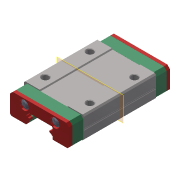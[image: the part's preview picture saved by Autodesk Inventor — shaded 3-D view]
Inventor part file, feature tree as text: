
AUTODESK INVENTOR PART (.ipt)
format: ipt  version: 2019.4 (Build 234330000, 330)  size: 473,600 bytes
history: imported  units: mm
features: other x9, plane x1, imported_body x1
ambient origin geometry x8: Origin, YZ Plane, XZ Plane, XY Plane, X Axis, Y Axis, Z Axis, Center Point
bodies: Solid1 (imported_parasolid), Solid2 (imported_parasolid), Solid3 (imported_parasolid), Solid4 (imported_parasolid), Solid5 (imported_parasolid), Solid6 (imported_parasolid), Solid7 (imported_parasolid), Solid8 (imported_parasolid), Solid9 (imported_parasolid)
feature tree (11):
  plane  "Work Plane1"
  other  "MID BODY, MGN 12H, LINEAR GUIDE BLOCK-1-solid1"
  other  "MID BODY, MGN 12H, LINEAR GUIDE BLOCK-1-solid2"
  other  "MID BODY, MGN 12H, LINEAR GUIDE BLOCK-1-solid3"
  other  "MID BODY, MGN 12H, LINEAR GUIDE BLOCK-1-solid4"
  other  "MID BODY, MGN 12H, LINEAR GUIDE BLOCK-1-solid5"
  other  "SCREW HEAD, MGN 12H, LINEAR GUIDE BLOCK-1-solid1"
  other  "SCREW HEAD, MGN 12H, LINEAR GUIDE BLOCK-2-solid1"
  other  "SCREW HEAD, MGN 12H, LINEAR GUIDE BLOCK-3-solid1"
  other  "SCREW HEAD, MGN 12H, LINEAR GUIDE BLOCK-4-solid1"
  imported_body  NMx_Import_Brep_tag  [imported B-rep: ~50 faces, bbox_mm=[19.044812, 8.226555, 32.4]]
